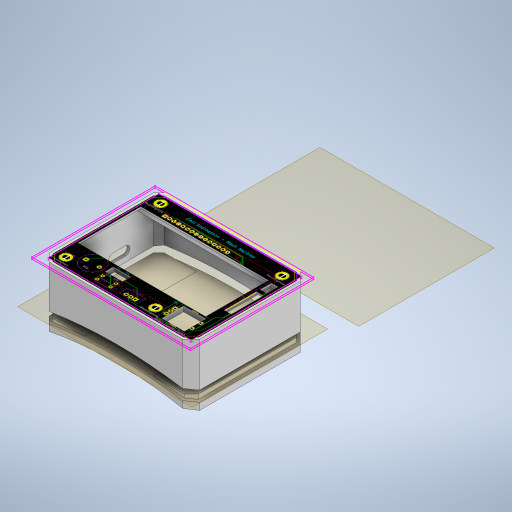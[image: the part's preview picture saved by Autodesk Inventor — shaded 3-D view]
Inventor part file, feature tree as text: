
AUTODESK INVENTOR PART (.ipt)
format: ipt  version: 2024 (Build 280153000, 153)  size: 747,008 bytes
history: native  units: mm
features: sketch x15, extrude x12, projected_geometry x5, plane x3, other x3
ambient origin geometry x8: Origin, YZ Plane, XZ Plane, XY Plane, X Axis, Y Axis, Z Axis, Center Point
bodies: Solid9 (feature_tree)
feature tree (38):
  extrude  "Extrusion14"  Depth=70.0mm
  plane  "Work Plane8"
  sketch  "Sketch23"  dims[d602=1.0mm d603=0.0mm d633=39.25mm]
  sketch  "3D Sketch1"
  other  "Decal3"
  extrude  "Extrusion16"  Depth=1.0mm
  extrude  "Extrusion17"  TaperAngle=45.0deg  [1 undecoded]
  extrude  "Extrusion18"  TaperAngle=135.0deg  [1 undecoded]
  sketch  "Sketch27"  dims[d686=0.5mm d687=0.5mm]
  extrude  "Extrusion20"  Depth=0.5mm
  extrude  "Extrusion21"  Depth=0.5mm
  extrude  "Extrusion22"  TaperAngle=135.0deg  [1 undecoded]
  extrude  "Extrusion23"  TaperAngle=135.0deg  [1 undecoded]
  sketch  "Sketch31"  dims[d698=1.5mm d699=1.5mm]
  plane  "Work Plane10"
  extrude  "Extrusion24"  Depth=1.5mm
  extrude  "Extrusion25"  Depth=1.5mm
  plane  "Work Plane11"
  extrude  "Extrusion26"  Depth=25.0mm TaperAngle=0.0deg
  extrude  "Extrusion27"  Depth=2.5mm
  sketch  "Sketch21"  dims[d597=90.0mm d598=70.0mm]
  other  "Image15"
  sketch  "Sketch24"  dims[d668=62.75mm d681=45.0deg]
  projected_geometry  "Projected Loop3"
  projected_geometry  "Projected Loop4"
  projected_geometry  "Projected Loop5"
  projected_geometry  "Projected Loop6"
  projected_geometry  "Projected Loop7"
  other  "Project from Sketch23"
  sketch  "Sketch25"  dims[d682=135.0deg d683=135.0deg]
  sketch  "Sketch26"  dims[d684=135.0deg d685=0.5mm]
  sketch  "Sketch28"  dims[d688=0.5mm d693=135.0deg]
  sketch  "Sketch29"  dims[d694=135.0deg d695=135.0deg]
  sketch  "Sketch30"  dims[d696=135.0deg d697=1.5mm]
  sketch  "Sketch32"  dims[d700=1.5mm d703=25.0mm d704=0.0mm]
  sketch  "Sketch33"  dims[d705=24.0mm d706=0.0mm d707=2.5mm]
  sketch  "Sketch34"  dims[d708=2.5mm]
  sketch  "Sketch35"  dims[d709=2.5mm d710=2.5mm d711=8.0mm d712=0.0mm d715=12.0mm d716=5.0mm d721=18.1mm d722=10.0mm d723=0.0mm d724=81.103353mm d725=25.0mm d726=0.0mm d728=2.0mm d729=0.0mm d730=1.0mm d731=1.0mm d733=24.0mm d735=240.0mm d736=0.0mm d737=0.0mm d738=1.0mm d739=1.0mm d740=1.0mm d742=90.0deg d743=10.0mm d744=0.0mm d746=4.0mm d747=240.0mm d748=10.0mm d749=0.0mm d750=90.0deg d751=3.0mm d752=0.0mm d753=4.0mm d754=0.0mm d727=0.5mm]
note: 4 required parameter values undecoded (feature->parameter linkage not recoverable at this tier; creation-order binding heuristic only, values carry confidence <= 0.55)
